# Revit family: РОСМА_ТермометрОбщетехническийСпециальный(Шток)
name_source: partatom
category: Арматура трубопроводов
revit_build: Autodesk Revit 2018 (Build: 20180423_1000(x64)
units: mm (PartAtom-declared; Revit-internal decimal feet)

## family parameters
Всегда вертикально = Да
На основе рабочей плоскости = Нет
Общий = Нет
При загрузке вырезать с полостями = Нет
Размер круглого соединителя = Использовать диаметр
Тип детали = Вставляется

## types (1)
- 23.220
    ADSK_Единица измерения = шт.
    ADSK_Количество = 1
    D = 50 мм
    D1 = 52 мм
    D2 = 51 мм
    D2/2 = 30 мм
    D4 = 4 мм
    Dgol = 18 мм
    Dполости_переднСт = 45 мм
    L = 150 мм
    L1 = 3 мм
    R1 шкала = 18 мм
    R2 шкала = 17 мм
    R_Logo = 10 мм
    S = 12 мм
    S1 = 14 мм
    URL = https://rosma.spb.ru
    b = 9 мм
    b-e = 3 мм
    e = 6 мм
    h_rezba = 15 мм
    Группа модели = Оборудование
    Диапазон раб. температур = от -10°С до +60°С
    Длина стрелки = 16 мм
    Изготовитель = ЗАО "РОСМА"
    Класс точности = 2,5
    Климатическое исполнение = Группа С2 по ГОСТ Р 52931; климатическое исполнение УХЛ категории 2.1 по ГОСТ 15150
    Код IP = IP43
    Межповерочный интервал = 3 года
    Описание = Тип БТ, серия 220. Биметаллический коррозионностойкий термометр со штоком в виде иглы (погружной термометр) предназначен для измерения температуры густых, сыпучих и вязких сред.
    Осевое присоединение = Да
    Присоединение = Шток в виде иглы
    Техническая документация = ТУ 4211-001-4719015564-2008
    лого_задн_стенка = Нет
